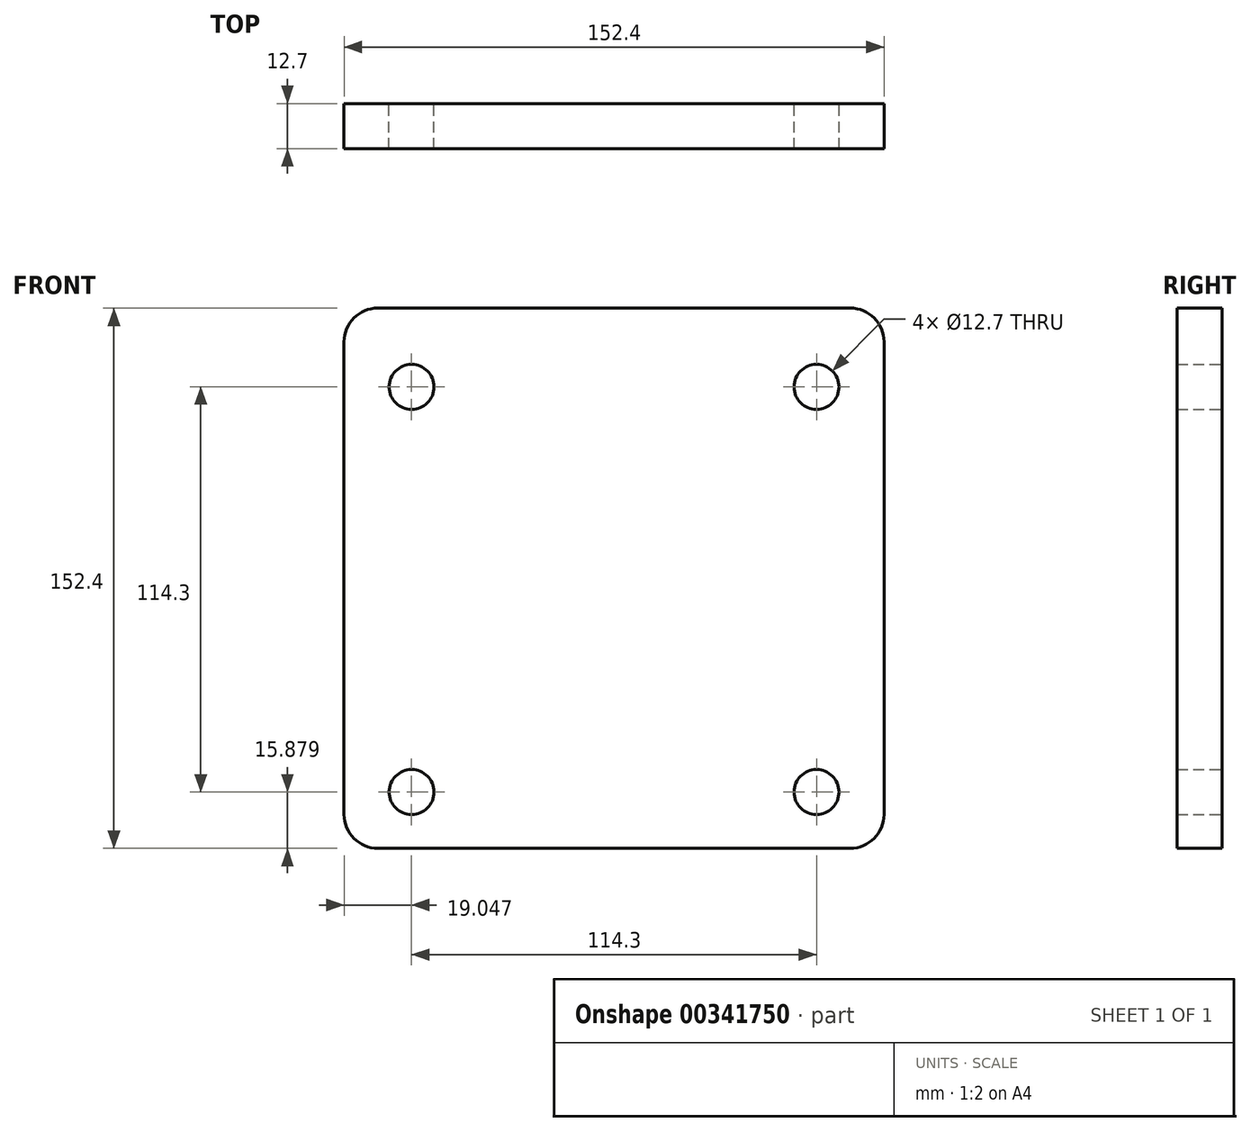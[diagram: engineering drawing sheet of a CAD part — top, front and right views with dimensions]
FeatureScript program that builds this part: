
annotation { "Feature Type Name" : "Feature", "Feature Type Description" : "" }
export const myFeature = defineFeature(function(context is Context, id is Id, definition is map)
    precondition{}
    {
        {
            var Q0;
            Q0=qCreatedBy(makeId("Front.planeOp"),FACE);
            var sketch = newSketch(context, id + "F0", { "sketchPlane" : qUnion([Q0])});
            skLineSegment(sketch, "E0.bottom", {"start": v(-62.73, 78.25) * mm, "end": v(70.62, 78.25) * mm});
            skLineSegment(sketch, "E0.top", {"start": v(-62.73, -74.15) * mm, "end": v(70.62, -74.15) * mm});
            skLineSegment(sketch, "E0.left", {"start": v(-72.25, 68.73) * mm, "end": v(-72.25, -64.62) * mm});
            skLineSegment(sketch, "E0.right", {"start": v(80.15, 68.73) * mm, "end": v(80.15, -64.62) * mm});
            skCircle(sketch, "E1", {"center": v(-53.2, 56.03) * mm, "radius": 6.35 * mm});
            skCircle(sketch, "E2", {"center": v(61.1, 56.03) * mm, "radius": 6.35 * mm});
            skCircle(sketch, "E3", {"center": v(-53.2, -58.27) * mm, "radius": 6.35 * mm});
            skLineSegment(sketch, "E4", {"start": v(80.15, -74.15) * mm, "end": v(80.15, -58.27) * mm, "construction": true});
            skCircle(sketch, "E5", {"center": v(61.1, -58.27) * mm, "radius": 6.35 * mm});
            skPoint(sketch, "E6.visualSharp", {"position": v(-72.25, 78.25) * mm});
            skArc(sketch, "E6.filletArc", {"start": v(-62.73, 78.25) * mm, "mid": v(-69.46, 75.46) * mm, "end": v(-72.25, 68.73) * mm});
            skPoint(sketch, "E7.visualSharp", {"position": v(-72.25, -74.15) * mm});
            skArc(sketch, "E7.filletArc", {"start": v(-72.25, -64.62) * mm, "mid": v(-69.46, -71.36) * mm, "end": v(-62.73, -74.15) * mm});
            skPoint(sketch, "E8.visualSharp", {"position": v(80.15, -74.15) * mm});
            skArc(sketch, "E8.filletArc", {"start": v(70.62, -74.15) * mm, "mid": v(77.36, -71.36) * mm, "end": v(80.15, -64.62) * mm});
            skPoint(sketch, "E9.visualSharp", {"position": v(80.15, 78.25) * mm});
            skArc(sketch, "E9.filletArc", {"start": v(80.15, 68.73) * mm, "mid": v(77.36, 75.46) * mm, "end": v(70.62, 78.25) * mm});
            skSolve(sketch);
        }
        {
            var Q0;
            Q0 = qSketchRegion(id + "F0", true);
            extrude(context, id + "F1", {"entities" : qUnion([Q0]), "depth" : 12.7 * mm});
        }
    });
